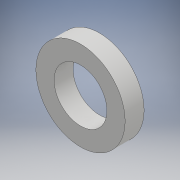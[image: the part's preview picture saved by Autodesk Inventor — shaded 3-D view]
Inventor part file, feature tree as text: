
AUTODESK INVENTOR PART (.ipt)
format: ipt  version: 2018 (Build 220112000, 112)  size: 100,352 bytes
history: native  units: mm
features: extrude x1, sketch x1
ambient origin geometry x8: Origin, YZ Plane, XZ Plane, XY Plane, X Axis, Y Axis, Z Axis, Center Point
bodies: Solid1 (feature_tree)
feature tree (2):
  extrude  "Extrusion1"  Depth=9.0mm
  sketch  "Sketch1"  dims[d0=42.25mm d1=25.0mm d2=9.0mm d3=0.0mm]
